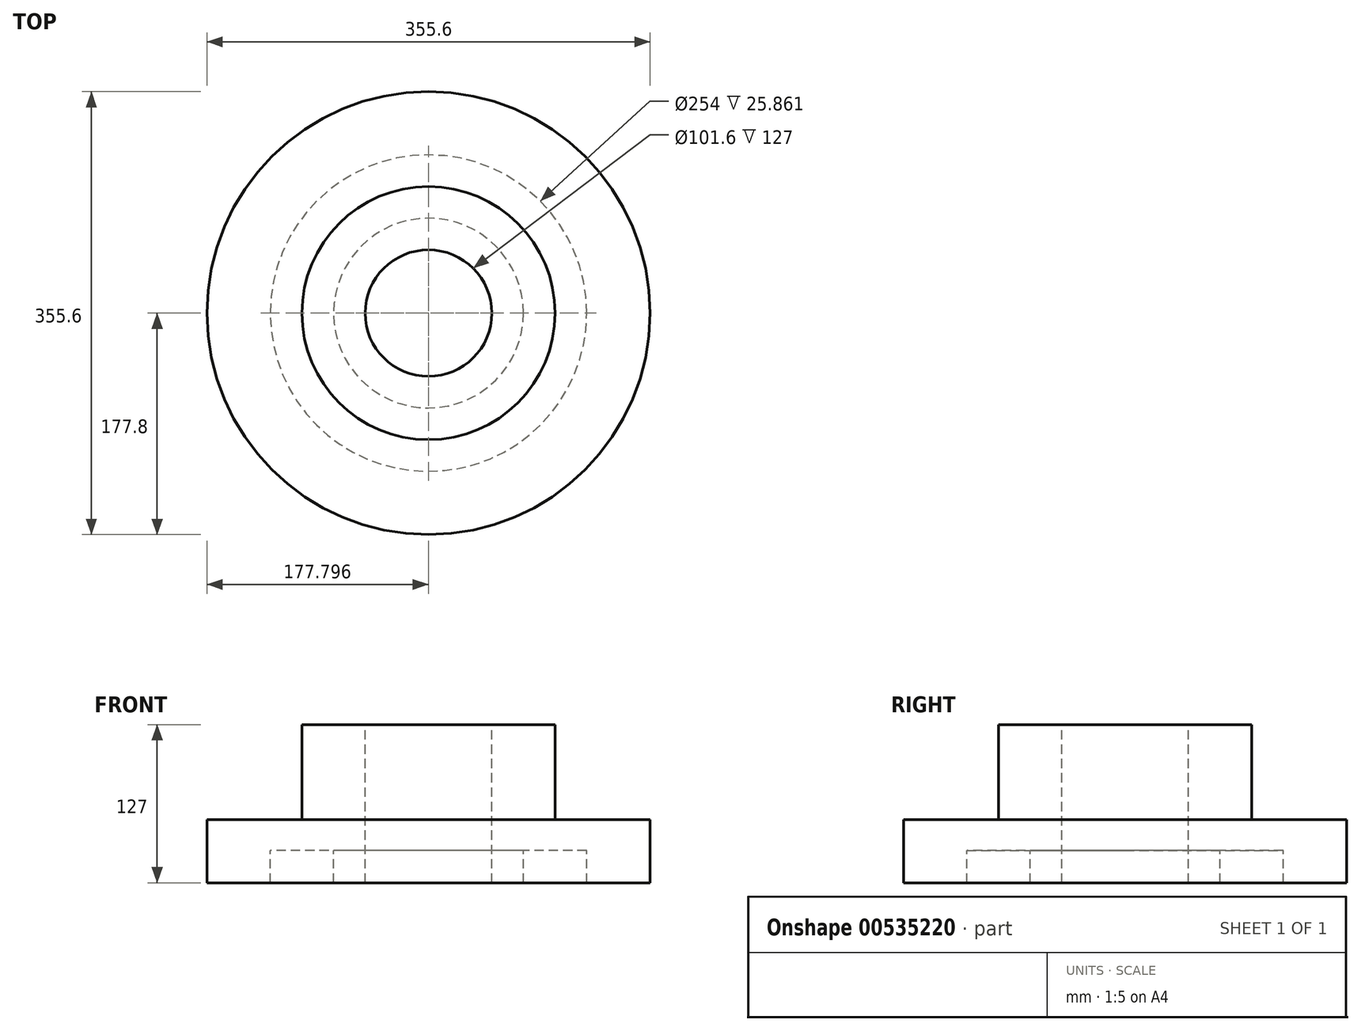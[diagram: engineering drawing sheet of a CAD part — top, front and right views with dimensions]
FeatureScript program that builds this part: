
annotation { "Feature Type Name" : "Feature", "Feature Type Description" : "" }
export const myFeature = defineFeature(function(context is Context, id is Id, definition is map)
    precondition{}
    {
        {
            var Q0;
            Q0=qCreatedBy(makeId("Front.planeOp"),FACE);
            var sketch = newSketch(context, id + "F0", { "sketchPlane" : qUnion([Q0])});
            skLineSegment(sketch, "E0", {"start": v(-57.73, 8.7) * mm, "end": v(-57.73, -42.1) * mm});
            skLineSegment(sketch, "E1", {"start": v(-57.73, -42.1) * mm, "end": v(-6.93, -42.1) * mm});
            skLineSegment(sketch, "E2", {"start": v(-6.93, -42.1) * mm, "end": v(-6.93, -16.23) * mm});
            skLineSegment(sketch, "E3", {"start": v(-6.93, -16.23) * mm, "end": v(43.87, -16.23) * mm});
            skLineSegment(sketch, "E4", {"start": v(43.87, -16.23) * mm, "end": v(43.87, -42.1) * mm});
            skLineSegment(sketch, "E5", {"start": v(43.87, -42.1) * mm, "end": v(69.27, -42.1) * mm});
            skLineSegment(sketch, "E6", {"start": v(69.27, -42.1) * mm, "end": v(69.27, 84.9) * mm});
            skLineSegment(sketch, "E7", {"start": v(69.27, 84.9) * mm, "end": v(18.47, 84.9) * mm});
            skLineSegment(sketch, "E8", {"start": v(18.47, 84.9) * mm, "end": v(18.47, 8.7) * mm});
            skLineSegment(sketch, "E9", {"start": v(18.47, 8.7) * mm, "end": v(-57.73, 8.7) * mm});
            skLineSegment(sketch, "E10", {"start": v(120.07, 97.96) * mm, "end": v(120.07, -67.52) * mm});
            skSolve(sketch);
        }
        {
            var Q0;
            Q0=makeQuery(id+"F0.imprint","IMPRINT",FACE,{"disambiguationData":[TD([[makeQuery(id+"F0.imprint","IMPRINT",EDGE,{"derivedFrom":sQuery(id+"F0.wireOp",EDGE,"E0")}),1.0]])]});
            var Q1;
            Q1=sQuery(id+"F0.wireOp",EDGE,"E10");
            var Q2;
            Q2=sQuery(id+"F0.wireOp",EDGE,"E9");
            var Q3;
            Q3=sQuery(id+"F0.wireOp",EDGE,"E8");
            var Q4;
            Q4=sQuery(id+"F0.wireOp",EDGE,"E7");
            var Q5;
            Q5=sQuery(id+"F0.wireOp",EDGE,"E6");
            var Q6;
            Q6=sQuery(id+"F0.wireOp",EDGE,"E3");
            var Q7;
            Q7=sQuery(id+"F0.wireOp",EDGE,"E5");
            var Q8;
            Q8=sQuery(id+"F0.wireOp",EDGE,"E4");
            var Q9;
            Q9=sQuery(id+"F0.wireOp",EDGE,"E2");
            var Q10;
            Q10=sQuery(id+"F0.wireOp",EDGE,"E1");
            var Q11;
            Q11=sQuery(id+"F0.wireOp",EDGE,"E0");
            var Q12;
            Q12=sQuery(id+"F0.wireOp",EDGE,"E10");
            revolve(context, id + "F1", {"entities" : qUnion([Q0]), "surfaceEntities" : qUnion([Q1, Q2, Q3, Q4, Q5, Q6, Q7, Q8, Q9, Q10, Q11]), "axis" : qUnion([Q12]), "revolveType" : RevolveType.FULL});
        }
    });
